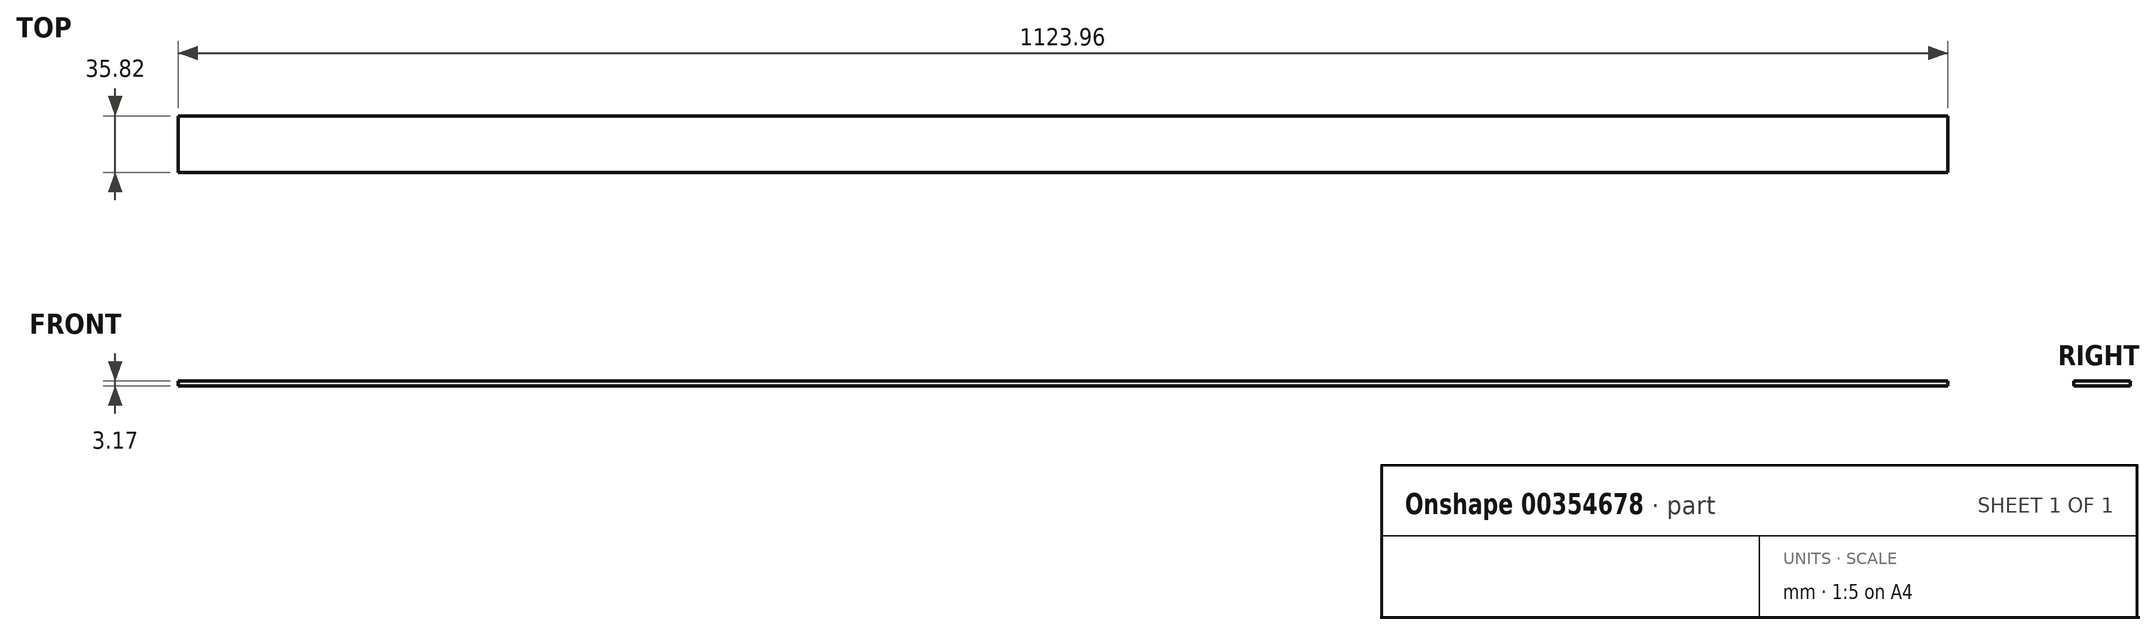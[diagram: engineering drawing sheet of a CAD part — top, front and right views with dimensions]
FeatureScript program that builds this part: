
annotation { "Feature Type Name" : "Feature", "Feature Type Description" : "" }
export const myFeature = defineFeature(function(context is Context, id is Id, definition is map)
    precondition{}
    {
        {
            var Q0;
            Q0=qCreatedBy(makeId("Top.planeOp"),FACE);
            var sketch = newSketch(context, id + "F0", { "sketchPlane" : qUnion([Q0])});
            skLineSegment(sketch, "E0.bottom", {"start": v(561.98, 17.9) * mm, "end": v(-561.98, 17.9) * mm});
            skLineSegment(sketch, "E0.top", {"start": v(561.98, -17.9) * mm, "end": v(-561.98, -17.9) * mm});
            skLineSegment(sketch, "E0.left", {"start": v(561.98, 17.9) * mm, "end": v(561.98, -17.9) * mm});
            skLineSegment(sketch, "E0.right", {"start": v(-561.98, 17.9) * mm, "end": v(-561.98, -17.9) * mm});
            skPoint(sketch, "E0.middle", {"position": v(0, 0) * mm});
            skSolve(sketch);
        }
        {
            var Q0;
            Q0=qSketchRegion(id+"F0",true);
            extrude(context, id + "F1", {"entities" : qUnion([Q0]), "depth" : 3.17 * mm});
        }
    });
